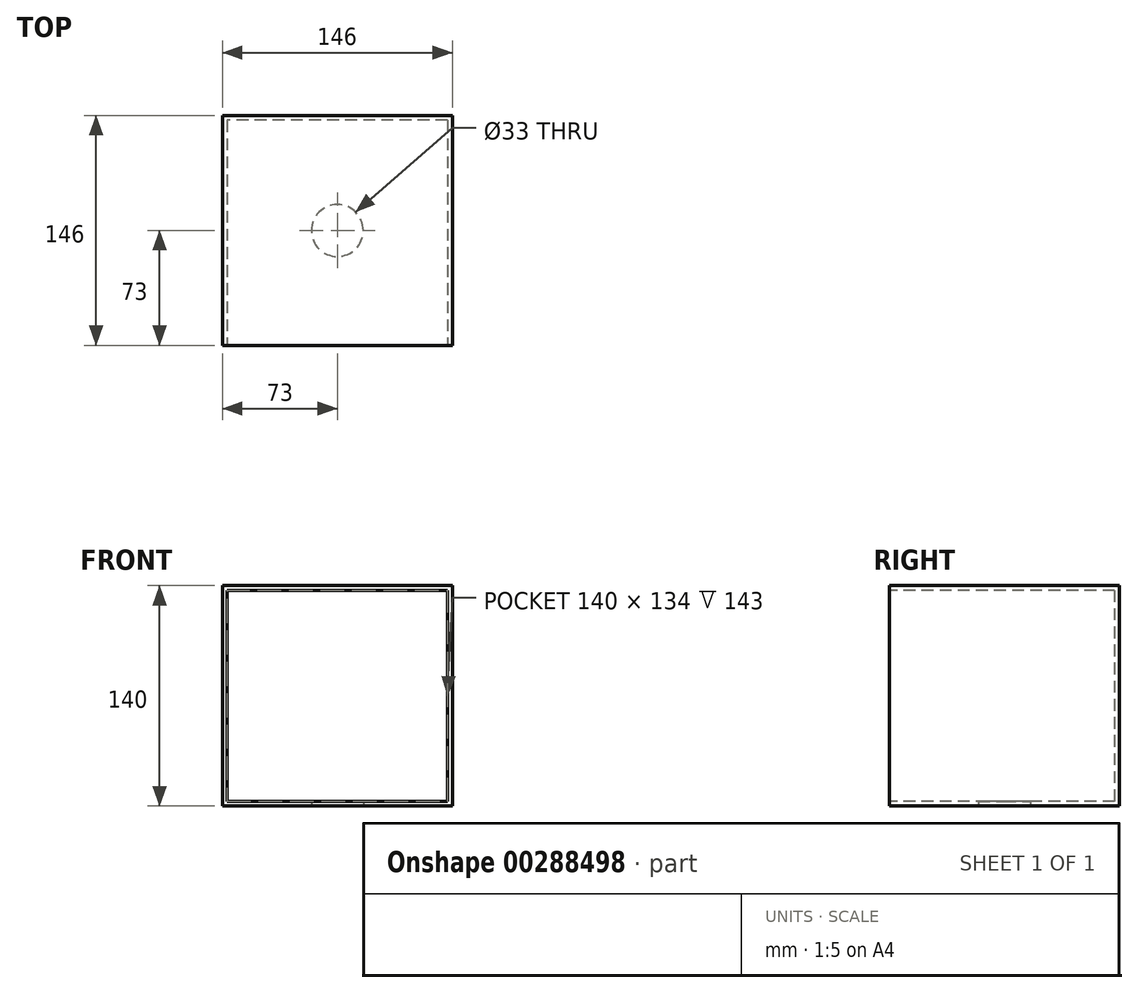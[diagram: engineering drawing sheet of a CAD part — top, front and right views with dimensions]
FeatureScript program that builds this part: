
annotation { "Feature Type Name" : "Feature", "Feature Type Description" : "" }
export const myFeature = defineFeature(function(context is Context, id is Id, definition is map)
    precondition{}
    {
        {
            var Q0;
            Q0=qCreatedBy(makeId("Top.planeOp"),FACE);
            var sketch = newSketch(context, id + "F0", { "sketchPlane" : qUnion([Q0])});
            skLineSegment(sketch, "E0.bottom", {"start": v(73, 73) * mm, "end": v(-73, 73) * mm});
            skLineSegment(sketch, "E0.top", {"start": v(73, -73) * mm, "end": v(-73, -73) * mm});
            skLineSegment(sketch, "E0.left", {"start": v(73, 73) * mm, "end": v(73, -73) * mm});
            skLineSegment(sketch, "E0.right", {"start": v(-73, 73) * mm, "end": v(-73, -73) * mm});
            skPoint(sketch, "E0.middle", {"position": v(0, 0) * mm});
            skCircle(sketch, "E1", {"center": v(0, 0) * mm, "radius": 16.5 * mm});
            skSolve(sketch);
        }
        {
            var Q0;
            Q0=makeQuery(id+"F0.imprint","IMPRINT",FACE,{"disambiguationData":[TD([[makeQuery(id+"F0.imprint","IMPRINT",EDGE,{"derivedFrom":sQuery(id+"F0.wireOp",EDGE,"E0.bottom")}),1.0]])]});
            var Q1;
            Q1=makeQuery(id+"F0.imprint","IMPRINT",FACE,{"disambiguationData":[TD([[makeQuery(id+"F0.imprint","IMPRINT",EDGE,{"derivedFrom":sQuery(id+"F0.wireOp",EDGE,"E1")}),1.0]])]});
            extrude(context, id + "F1", {"entities" : qUnion([Q0, Q1]), "depth" : 140 * mm});
        }
        {
            var Q0;
            Q0=makeQuery(id+"F1.opExtrude","SWEPT_FACE",FACE,{"disambiguationData":[OSD([sQuery(id+"F0.wireOp",EDGE,"E0.top")])]});
            shell(context, id + "F2", {"entities" : qUnion([Q0]), "thickness" : 3 * mm});
        }
        {
            var Q0;
            Q0=makeQuery(id+"F0.imprint","IMPRINT",FACE,{"disambiguationData":[TD([[makeQuery(id+"F0.imprint","IMPRINT",EDGE,{"derivedFrom":sQuery(id+"F0.wireOp",EDGE,"E1")}),1.0]])]});
            extrude(context, id + "F3", {"entities" : qUnion([Q0]), "operationType" : NewBodyOperationType.REMOVE, "depth" : 3 * mm});
        }
    });
